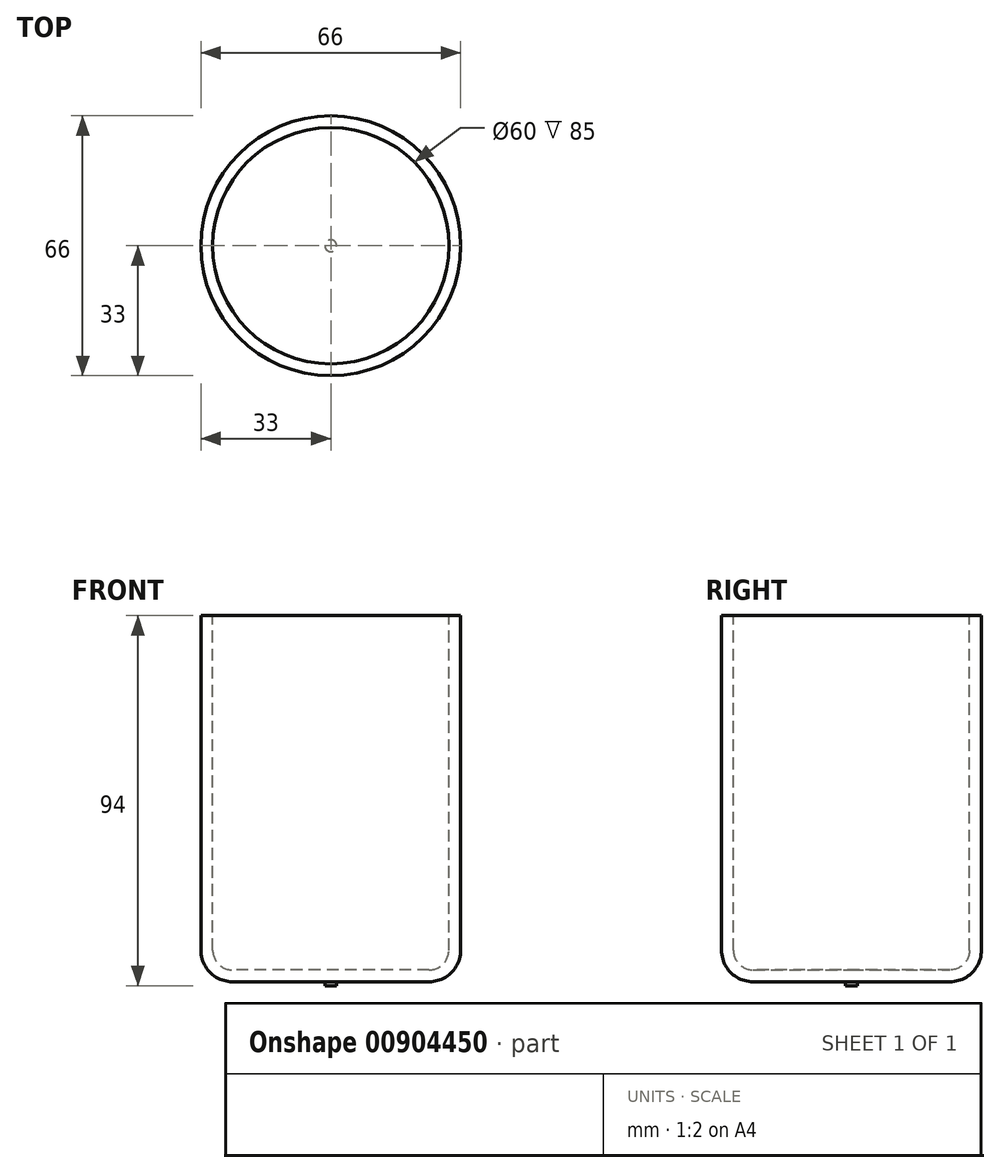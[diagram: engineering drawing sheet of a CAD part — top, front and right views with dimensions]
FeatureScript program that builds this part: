
annotation { "Feature Type Name" : "Feature", "Feature Type Description" : "" }
export const myFeature = defineFeature(function(context is Context, id is Id, definition is map)
    precondition{}
    {
        {
            var Q0;
            Q0=qCreatedBy(makeId("Front.planeOp"),FACE);
            var sketch = newSketch(context, id + "F0", { "sketchPlane" : qUnion([Q0])});
            skLineSegment(sketch, "E0", {"start": v(0, 0) * mm, "end": v(25, 0) * mm});
            skLineSegment(sketch, "E1", {"start": v(33, 8) * mm, "end": v(33, 93) * mm});
            skLineSegment(sketch, "E2", {"start": v(33, 93) * mm, "end": v(30, 93) * mm});
            skLineSegment(sketch, "E3", {"start": v(30, 93) * mm, "end": v(30, 8) * mm});
            skLineSegment(sketch, "E4", {"start": v(25, 3) * mm, "end": v(0, 3) * mm});
            skLineSegment(sketch, "E5", {"start": v(0, 3) * mm, "end": v(0, 0) * mm});
            skLineSegment(sketch, "E6", {"start": v(0, -4.15) * mm, "end": v(0, 19.31) * mm, "construction": true});
            skPoint(sketch, "E7.visualSharp", {"position": v(30, 3) * mm});
            skArc(sketch, "E7.filletArc", {"start": v(25, 3) * mm, "mid": v(28.54, 4.46) * mm, "end": v(30, 8) * mm});
            skPoint(sketch, "E8.visualSharp", {"position": v(33, 0) * mm});
            skArc(sketch, "E9.filletArc", {"start": v(25, 0) * mm, "mid": v(30.66, 2.34) * mm, "end": v(33, 8) * mm});
            skSolve(sketch);
        }
        {
            var Q0;
            Q0 = qSketchRegion(id + "F0", true);
            var Q1;
            Q1=sQuery(id+"F0.wireOp",EDGE,"E6");
            revolve(context, id + "F1", {"surfaceOperationType" : NewSurfaceOperationType.NEW, "entities" : qUnion([Q0]), "axis" : qUnion([Q1]), "revolveType" : RevolveType.FULL, "oppositeDirection" : true});
        }
        {
            var Q0;
            Q0=makeQuery(id+"F1.opRevolve","SWEPT_FACE",FACE,{"disambiguationData":[OSD([sQuery(id+"F0.wireOp",EDGE,"E0")])]});
            var sketch = newSketch(context, id + "F2", { "sketchPlane" : qUnion([Q0])});
            skCircle(sketch, "E10", {"center": v(0, 0) * mm, "radius": 1.5 * mm});
            skSolve(sketch);
        }
        {
            var Q0;
            Q0 = qSketchRegion(id + "F2", true);
            extrude(context, id + "F3", {"entities" : qUnion([Q0]), "operationType" : NewBodyOperationType.ADD, "depth" : 1 * mm, "offsetDistance" : 25 * mm});
        }
    });
